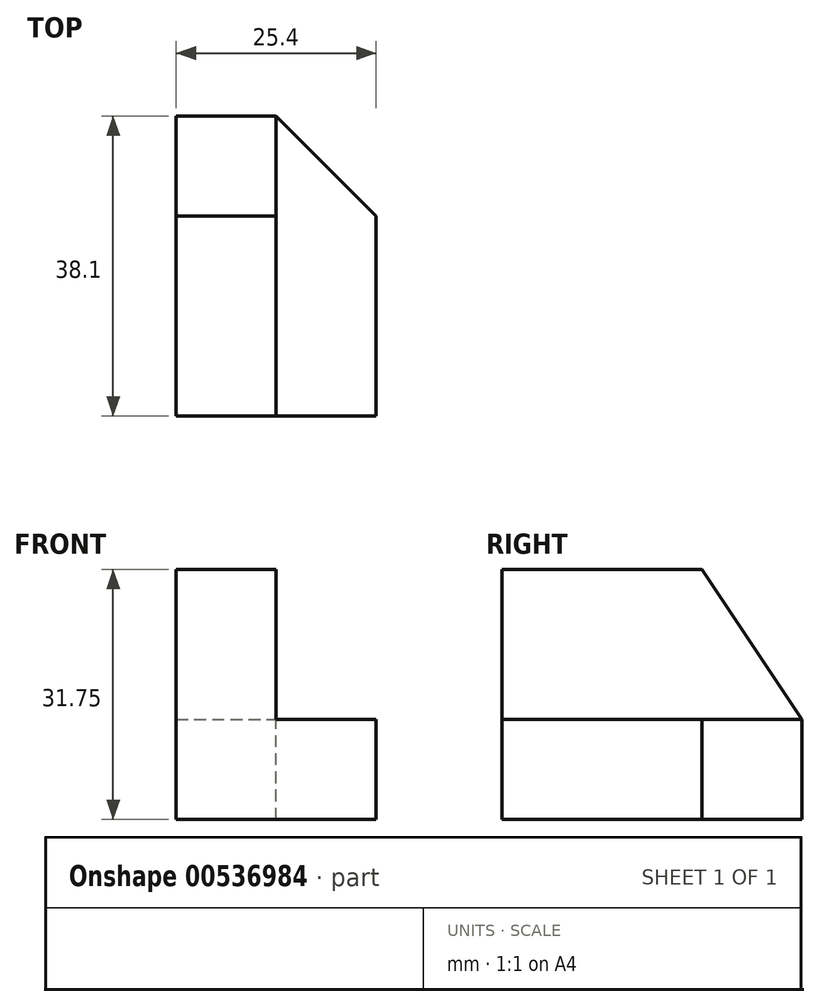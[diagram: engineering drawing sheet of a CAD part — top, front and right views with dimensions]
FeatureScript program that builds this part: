
annotation { "Feature Type Name" : "Feature", "Feature Type Description" : "" }
export const myFeature = defineFeature(function(context is Context, id is Id, definition is map)
    precondition{}
    {
        {
            var Q0;
            Q0=qCreatedBy(makeId("Front.planeOp"),FACE);
            var sketch = newSketch(context, id + "F0", { "sketchPlane" : qUnion([Q0])});
            skLineSegment(sketch, "E0", {"start": v(41.35, 39.7) * mm, "end": v(41.35, 20.65) * mm});
            skLineSegment(sketch, "E1", {"start": v(41.35, 20.65) * mm, "end": v(54.05, 20.65) * mm});
            skLineSegment(sketch, "E2", {"start": v(54.05, 20.65) * mm, "end": v(54.05, 7.95) * mm});
            skLineSegment(sketch, "E3", {"start": v(54.05, 7.95) * mm, "end": v(28.65, 7.95) * mm});
            skLineSegment(sketch, "E4", {"start": v(28.65, 7.95) * mm, "end": v(28.65, 39.7) * mm});
            skLineSegment(sketch, "E5", {"start": v(28.65, 39.7) * mm, "end": v(41.35, 39.7) * mm});
            skSolve(sketch);
        }
        {
            var Q0;
            Q0=makeQuery(id+"F0.imprint","IMPRINT",FACE,{"disambiguationData":[TD([[makeQuery(id+"F0.imprint","IMPRINT",EDGE,{"derivedFrom":sQuery(id+"F0.wireOp",EDGE,"E0")}),-1.0]])]});
            extrude(context, id + "F1", {"entities" : qUnion([Q0]), "depth" : 38.1 * mm, "offsetDistance" : 25.4 * mm});
        }
        {
            var Q0;
            Q0=makeQuery(id+"F1.opExtrude","SWEPT_FACE",FACE,{"disambiguationData":[OSD([sQuery(id+"F0.wireOp",EDGE,"E1")])]});
            var sketch = newSketch(context, id + "F2", { "sketchPlane" : qUnion([Q0])});
            skLineSegment(sketch, "E6", {"start": v(41.35, 0) * mm, "end": v(54.05, -12.7) * mm});
            skSolve(sketch);
        }
        {
            var Q0;
            {var subQ0=sQuery(id+"F2.wireOp",EDGE,"E6");Q0=makeQuery(id+"F2.imprint","IMPRINT",FACE,{"disambiguationData":[TD([[makeQuery(id+"F2.imprint","IMPRINT",EDGE,{"derivedFrom":subQ0}),1.0]])]});}
            extrude(context, id + "F3", {"entities" : qUnion([Q0]), "operationType" : NewBodyOperationType.REMOVE, "endBound" : BoundingType.THROUGH_ALL, "oppositeDirection" : true, "depth" : 25.4 * mm, "offsetDistance" : 25.4 * mm});
        }
        {
            var Q0;
            Q0=makeQuery(id+"F1.opExtrude","SWEPT_FACE",FACE,{"disambiguationData":[OSD([sQuery(id+"F0.wireOp",EDGE,"E0")])]});
            var sketch = newSketch(context, id + "F4", { "sketchPlane" : qUnion([Q0])});
            skLineSegment(sketch, "E7", {"start": v(-12.7, 39.7) * mm, "end": v(0, 20.65) * mm});
            skSolve(sketch);
        }
        {
            var Q0;
            {var subQ0=sQuery(id+"F4.wireOp",EDGE,"E7");Q0=makeQuery(id+"F4.imprint","IMPRINT",FACE,{"disambiguationData":[TD([[makeQuery(id+"F4.imprint","IMPRINT",EDGE,{"derivedFrom":subQ0}),1.0]])]});}
            extrude(context, id + "F5", {"entities" : qUnion([Q0]), "operationType" : NewBodyOperationType.REMOVE, "endBound" : BoundingType.THROUGH_ALL, "oppositeDirection" : true, "depth" : 25.4 * mm, "offsetDistance" : 25.4 * mm});
        }
    });
